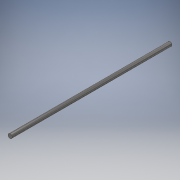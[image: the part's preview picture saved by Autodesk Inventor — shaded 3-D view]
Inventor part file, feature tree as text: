
AUTODESK INVENTOR PART (.ipt)
format: ipt  version: 2017.3 (Build 213256000, 256)  size: 93,696 bytes
history: native  units: mm
features: extrude x1, thread x1, sketch x1
ambient origin geometry x8: Origin, YZ Plane, XZ Plane, XY Plane, X Axis, Y Axis, Z Axis, Center Point
bodies: Solid1 (feature_tree)
feature tree (3):
  extrude  "Extrusion1"  Depth=300.0mm TaperAngle=0.0deg
  thread  "Thread1"  [1 undecoded]
  sketch  "Sketch1"  dims[d0=8.0mm d1=300.0mm d2=0.0mm d3=10.0mm d4=0.0mm]
note: 1 required parameter value undecoded (feature->parameter linkage not recoverable at this tier; creation-order binding heuristic only, values carry confidence <= 0.55)
